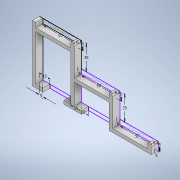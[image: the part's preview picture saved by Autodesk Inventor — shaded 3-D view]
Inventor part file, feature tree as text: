
AUTODESK INVENTOR PART (.ipt)
format: ipt  version: 2020 (Build 240168000, 168)  size: 164,352 bytes
history: native  units: mm
features: extrude x1, chamfer x1, sketch x1
ambient origin geometry x8: Origin, YZ Plane, XZ Plane, XY Plane, X Axis, Y Axis, Z Axis, Center Point
bodies: Solid1 (feature_tree)
feature tree (3):
  extrude  "Extrusion1"  Depth=6.6mm
  chamfer  "Chamfer1"  Distance=5.0mm
  sketch  "Sketch1"  dims[d0=50.0mm d1=6.6mm d9=5.0mm d10=35.0mm d11=50.0mm d12=6.6mm d13=5.0mm d14=5.0mm d15=5.0mm d16=35.0mm d17=50.0mm d18=6.6mm d19=5.0mm d20=5.0mm d21=5.0mm d22=10.0mm d23=0.0mm d24=15.0mm d25=15.0mm d26=15.0mm d27=2.0mm d28=2.0mm d29=45.0deg]
